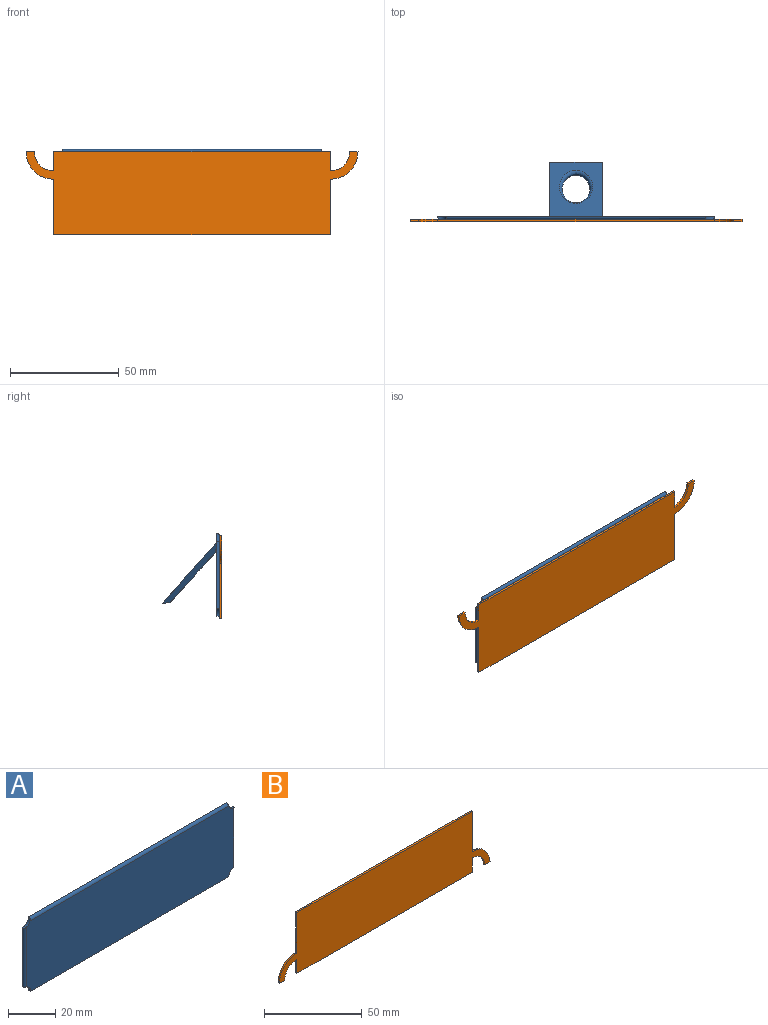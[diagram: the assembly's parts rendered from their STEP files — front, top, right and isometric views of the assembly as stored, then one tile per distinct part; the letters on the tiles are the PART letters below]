
ASSEMBLY  parts=2 mates=1
PART A: 19 faces, bbox 127.4x26.8x38.5 mm
  f0: plane 19.06x8.98mm, normal (0,-0.74,-0.67), area 83.7mm2, adj f5,f15,f16,f18
  f1: plane 119.37x1.27mm, normal (0,0,-1), area 151.6mm2, adj f2,f3,f9,f10
  f2: plane 127x38.1mm, normal (0,1,0), area 4790.2mm2, adj f1,f4,f5,f7,f8,f9,f10,f11
  f3: plane 124.46x36.83mm, normal (0,-1,0), area 4562.4mm2, adj f1,f7,f8,f9,f10,f11,f12,f13
  f4: plane 27.83x25.06mm, normal (0,0.74,0.67), area 627.5mm2, adj f2,f14,f16,f17,f18
  f5: plane 24.07x4.48mm, normal (0,-0.99,-0.15), area 97.6mm2, adj f0,f2,f16,f18
  f6: plane 19.06x9.89mm, normal (0,-0.74,-0.67), area 97.7mm2, adj f15,f16,f17,f18
  f7: cylinder r=3.81mm len=3.99mm, axis (0,-1,0), area 6.4mm2, adj f2,f3,f11,f13
  f8: cylinder r=3.81mm len=3.89mm, axis (0,-1,0), area 6.1mm2, adj f2,f3,f11,f12
  f9: cylinder r=3.81mm len=3.82mm, axis (0,-1,0), area 6.8mm2, adj f1,f2,f3,f12
  f10: cylinder r=3.81mm len=3.82mm, axis (0,-1,0), area 6.8mm2, adj f1,f2,f3,f13
  f11: cylinder r=1.27mm len=119.5mm, axis (-1,0,0), area 238mm2, adj f2,f3,f7,f8
  f12: cylinder r=1.27mm len=30.87mm, axis (0,0,-1), area 61.2mm2, adj f2,f3,f8,f9
  f13: cylinder r=1.27mm len=30.69mm, axis (0,0,1), area 60.8mm2, adj f2,f3,f7,f10
  f14: bspline ~17.9x15.34mm, area 114.9mm2, adj f4,f15
  f15: bspline ~19.94x19.49mm, area 221.5mm2, adj f0,f6,f14,f16,f18
  f16: plane 28.26x25.49mm, normal (-0.71,-0.53,-0.47), area 123.1mm2, adj f0,f2,f4,f5,f6,f15,f17
  f17: plane 24.13x3.59mm, normal (0,-0.05,-1), area 77.6mm2, adj f4,f6,f16,f18
  f18: plane 28.26x25.49mm, normal (0.71,-0.53,-0.47), area 123.1mm2, adj f0,f2,f4,f5,f6,f15,f17
PART B: 14 faces, bbox 152.4x1x38.1 mm
  f0: cylinder r=12.7mm len=12.7mm, axis (0,-1,0), area 20.3mm2, adj f1,f11,f12,f13
  f1: plane 25.4x1.02mm, normal (1,0,0), area 25.8mm2, adj f0,f2,f12,f13
  f2: plane 127x1.02mm, normal (0,0,1), area 129mm2, adj f1,f3,f12,f13
  f3: plane 25.4x1.02mm, normal (-1,0,0), area 25.8mm2, adj f2,f4,f12,f13
  f4: cylinder r=12.7mm len=12.7mm, axis (0,-1,0), area 20.3mm2, adj f3,f5,f12,f13
  f5: plane 3.81x1.02mm, normal (0,0,-1), area 3.9mm2, adj f4,f6,f12,f13
  f6: cylinder r=8.89mm len=8.89mm, axis (0,-1,0), area 14.2mm2, adj f5,f7,f12,f13
  f7: plane 8.89x1.02mm, normal (-1,0,0), area 9mm2, adj f6,f8,f12,f13
  f8: plane 127x1.02mm, normal (0,0,-1), area 129mm2, adj f7,f9,f12,f13
  f9: plane 8.89x1.02mm, normal (1,0,0), area 9mm2, adj f8,f10,f12,f13
  f10: cylinder r=8.89mm len=8.89mm, axis (0,-1,0), area 14.2mm2, adj f9,f11,f12,f13
  f11: plane 3.81x1.02mm, normal (0,0,-1), area 3.9mm2, adj f0,f10,f12,f13
  f12: plane 152.4x38.1mm, normal (0,1,0), area 4967.9mm2, adj f0,f1,f2,f3,f4,f5,f6,f7
  f13: plane 152.4x38.1mm, normal (0,-1,0), area 4967.9mm2, adj f0,f1,f2,f3,f4,f5,f6,f7
PLACE A t=(0.01,2.29,0.3)mm fixed
PLACE B rot(axis=(0,1,0),180deg) t=(0,0,-0.63)mm
MATE slider A.f3 <-> B.f12  axis (0,-1,0) through (0,2.29,-0.31)mm
